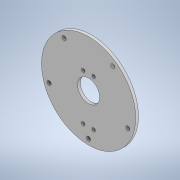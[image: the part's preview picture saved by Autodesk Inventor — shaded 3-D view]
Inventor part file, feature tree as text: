
AUTODESK INVENTOR PART (.ipt)
format: ipt  version: 2022 (Build 260153000, 153)  size: 138,240 bytes
history: native  units: mm
features: extrude x1
ambient origin geometry x8: Origin, YZ Plane, XZ Plane, XY Plane, X Axis, Y Axis, Z Axis, Center Point
bodies: Solid1 (feature_tree)
feature tree (1):
  extrude  "Extrusion1"  Depth=100.0mm
